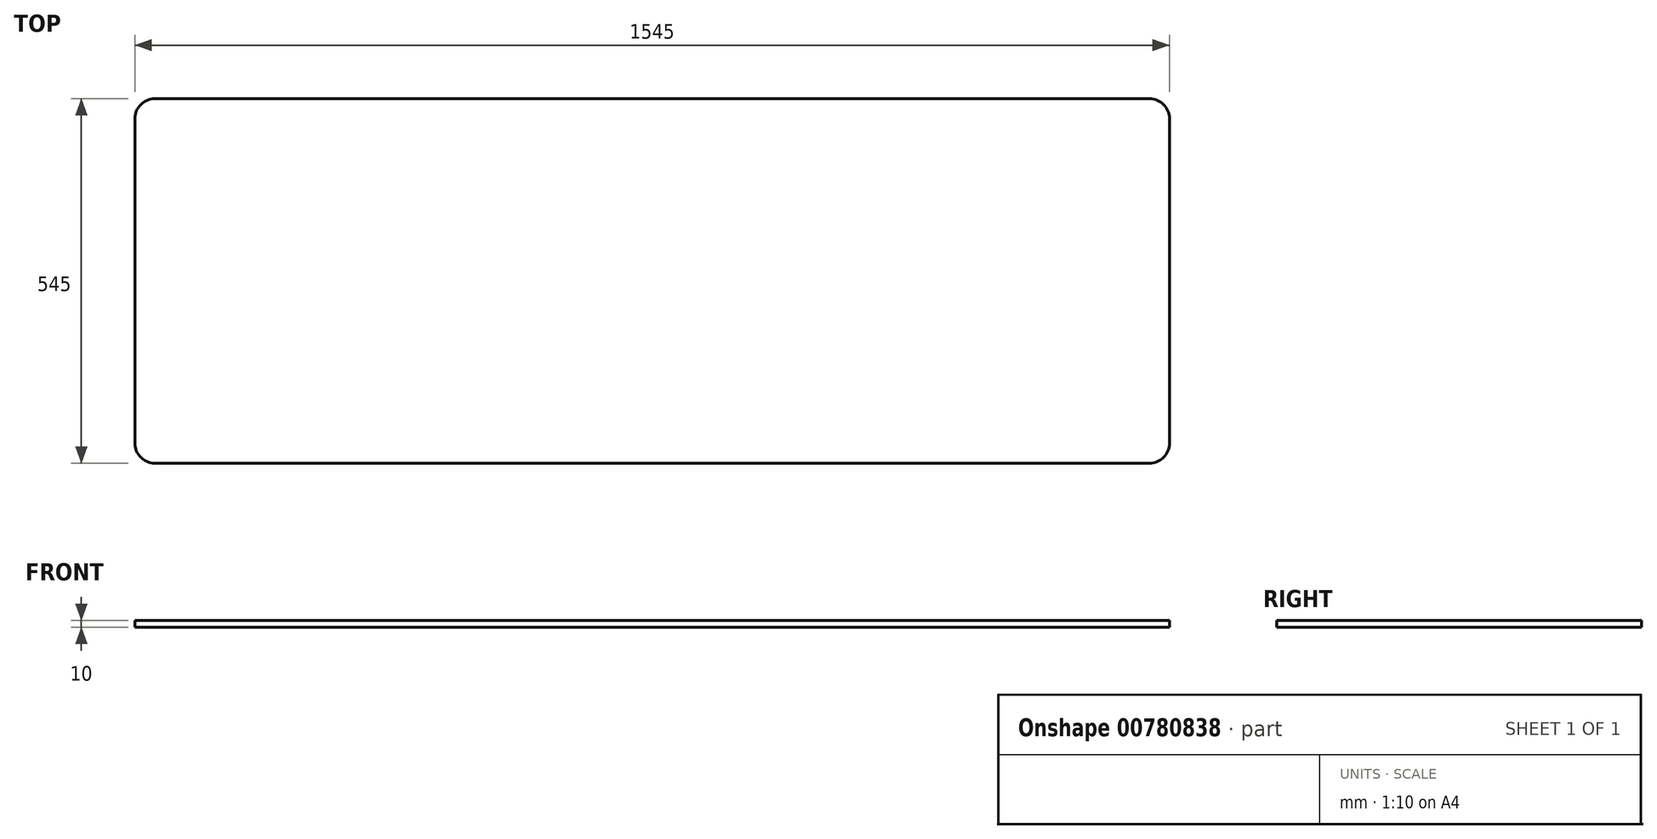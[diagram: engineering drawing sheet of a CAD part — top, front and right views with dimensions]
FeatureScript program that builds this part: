
annotation { "Feature Type Name" : "Feature", "Feature Type Description" : "" }
export const myFeature = defineFeature(function(context is Context, id is Id, definition is map)
    precondition{}
    {
        {
            var Q0;
            Q0=qCreatedBy(makeId("Top.planeOp"),FACE);
            var sketch = newSketch(context, id + "F0", { "sketchPlane" : qUnion([Q0])});
            skLineSegment(sketch, "E0.bottom", {"start": v(-742.5, 272.5) * mm, "end": v(742.5, 272.5) * mm});
            skLineSegment(sketch, "E0.top", {"start": v(-742.5, -272.5) * mm, "end": v(742.5, -272.5) * mm});
            skLineSegment(sketch, "E0.left", {"start": v(-772.5, 242.5) * mm, "end": v(-772.5, -242.5) * mm});
            skLineSegment(sketch, "E0.right", {"start": v(772.5, 242.5) * mm, "end": v(772.5, -242.5) * mm});
            skPoint(sketch, "E0.middle", {"position": v(0, 0) * mm});
            skPoint(sketch, "E1.visualSharp", {"position": v(-772.5, 272.5) * mm});
            skArc(sketch, "E1.filletArc", {"start": v(-742.5, 272.5) * mm, "mid": v(-763.71, 263.71) * mm, "end": v(-772.5, 242.5) * mm});
            skPoint(sketch, "E2.visualSharp", {"position": v(-772.5, -272.5) * mm});
            skArc(sketch, "E2.filletArc", {"start": v(-772.5, -242.5) * mm, "mid": v(-763.71, -263.71) * mm, "end": v(-742.5, -272.5) * mm});
            skPoint(sketch, "E3.visualSharp", {"position": v(772.5, 272.5) * mm});
            skArc(sketch, "E3.filletArc", {"start": v(772.5, 242.5) * mm, "mid": v(763.71, 263.71) * mm, "end": v(742.5, 272.5) * mm});
            skPoint(sketch, "E4.visualSharp", {"position": v(772.5, -272.5) * mm});
            skArc(sketch, "E4.filletArc", {"start": v(742.5, -272.5) * mm, "mid": v(763.71, -263.71) * mm, "end": v(772.5, -242.5) * mm});
            skSolve(sketch);
        }
        {
            var Q0;
            Q0 = qSketchRegion(id + "F0", true);
            extrude(context, id + "F1", {"entities" : qUnion([Q0]), "oppositeDirection" : true, "depth" : 10 * mm, "offsetDistance" : 25 * mm});
        }
    });
